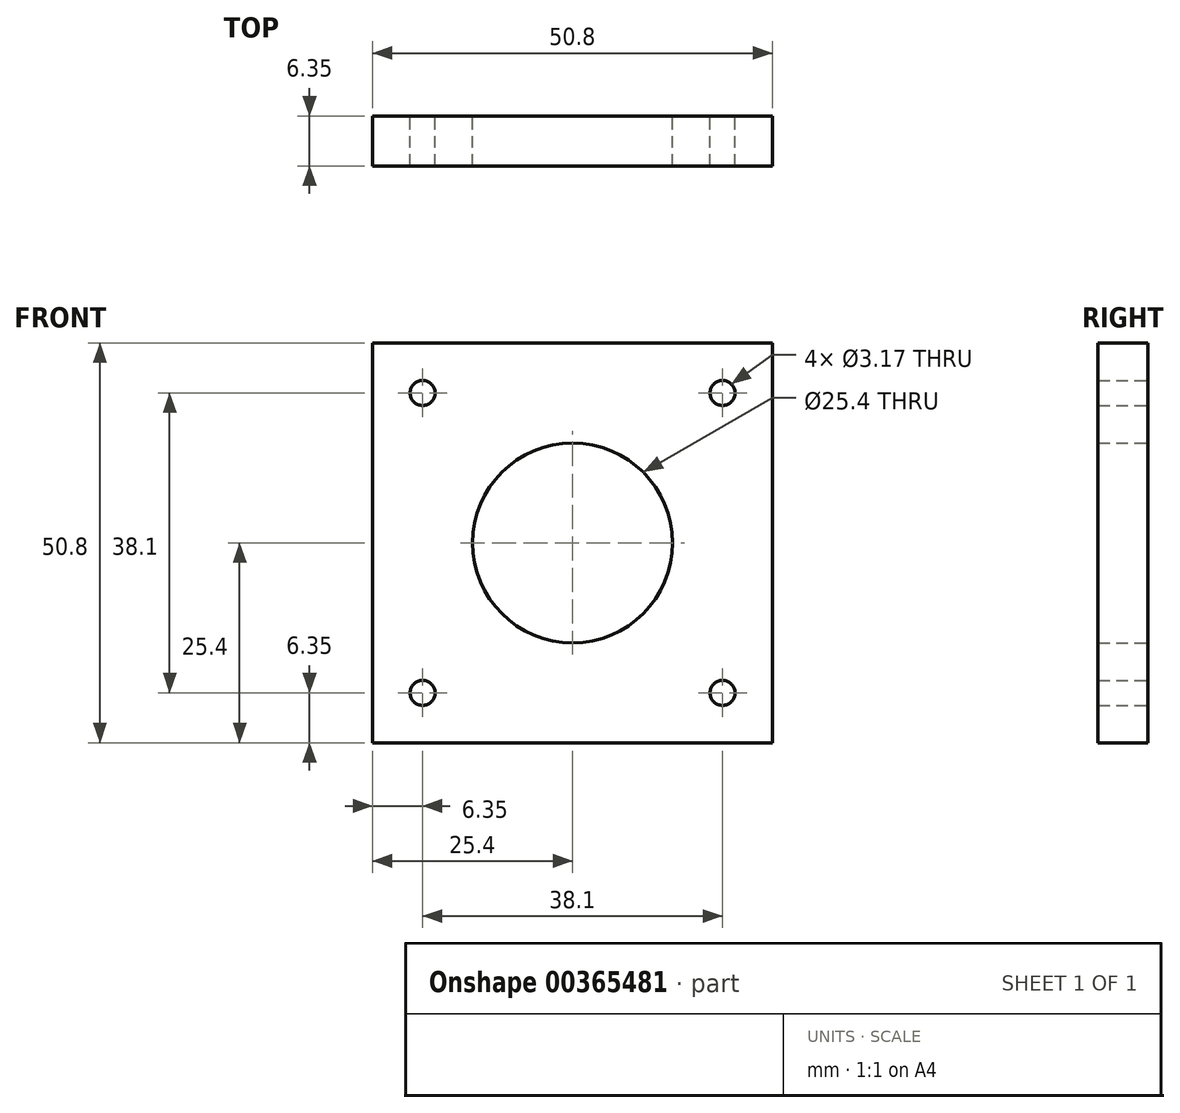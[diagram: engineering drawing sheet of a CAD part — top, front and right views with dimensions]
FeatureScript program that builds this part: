
annotation { "Feature Type Name" : "Feature", "Feature Type Description" : "" }
export const myFeature = defineFeature(function(context is Context, id is Id, definition is map)
    precondition{}
    {
        {
            var Q0;
            Q0=qCreatedBy(makeId("Front.planeOp"),FACE);
            var sketch = newSketch(context, id + "F0", { "sketchPlane" : qUnion([Q0])});
            skLineSegment(sketch, "E0.bottom", {"start": v(25.4, -25.4) * mm, "end": v(-25.4, -25.4) * mm});
            skLineSegment(sketch, "E0.top", {"start": v(25.4, 25.4) * mm, "end": v(-25.4, 25.4) * mm});
            skLineSegment(sketch, "E0.left", {"start": v(25.4, -25.4) * mm, "end": v(25.4, 25.4) * mm});
            skLineSegment(sketch, "E0.right", {"start": v(-25.4, -25.4) * mm, "end": v(-25.4, 25.4) * mm});
            skPoint(sketch, "E0.middle", {"position": v(0, 0) * mm});
            skCircle(sketch, "E1", {"center": v(-19.05, 19.05) * mm, "radius": 1.59 * mm});
            skCircle(sketch, "E2", {"center": v(19.05, 19.05) * mm, "radius": 1.59 * mm});
            skCircle(sketch, "E3", {"center": v(-19.05, -19.05) * mm, "radius": 1.59 * mm});
            skCircle(sketch, "E4", {"center": v(19.05, -19.05) * mm, "radius": 1.59 * mm});
            skCircle(sketch, "E5", {"center": v(0, 0) * mm, "radius": 12.7 * mm});
            skSolve(sketch);
        }
        {
            var Q0;
            Q0=makeQuery(id+"F0.imprint","IMPRINT",FACE,{"disambiguationData":[TD([[makeQuery(id+"F0.imprint","IMPRINT",EDGE,{"derivedFrom":sQuery(id+"F0.wireOp",EDGE,"E0.bottom")}),-1.0]])]});
            extrude(context, id + "F1", {"entities" : qUnion([Q0]), "depth" : 6.35 * mm});
        }
    });
